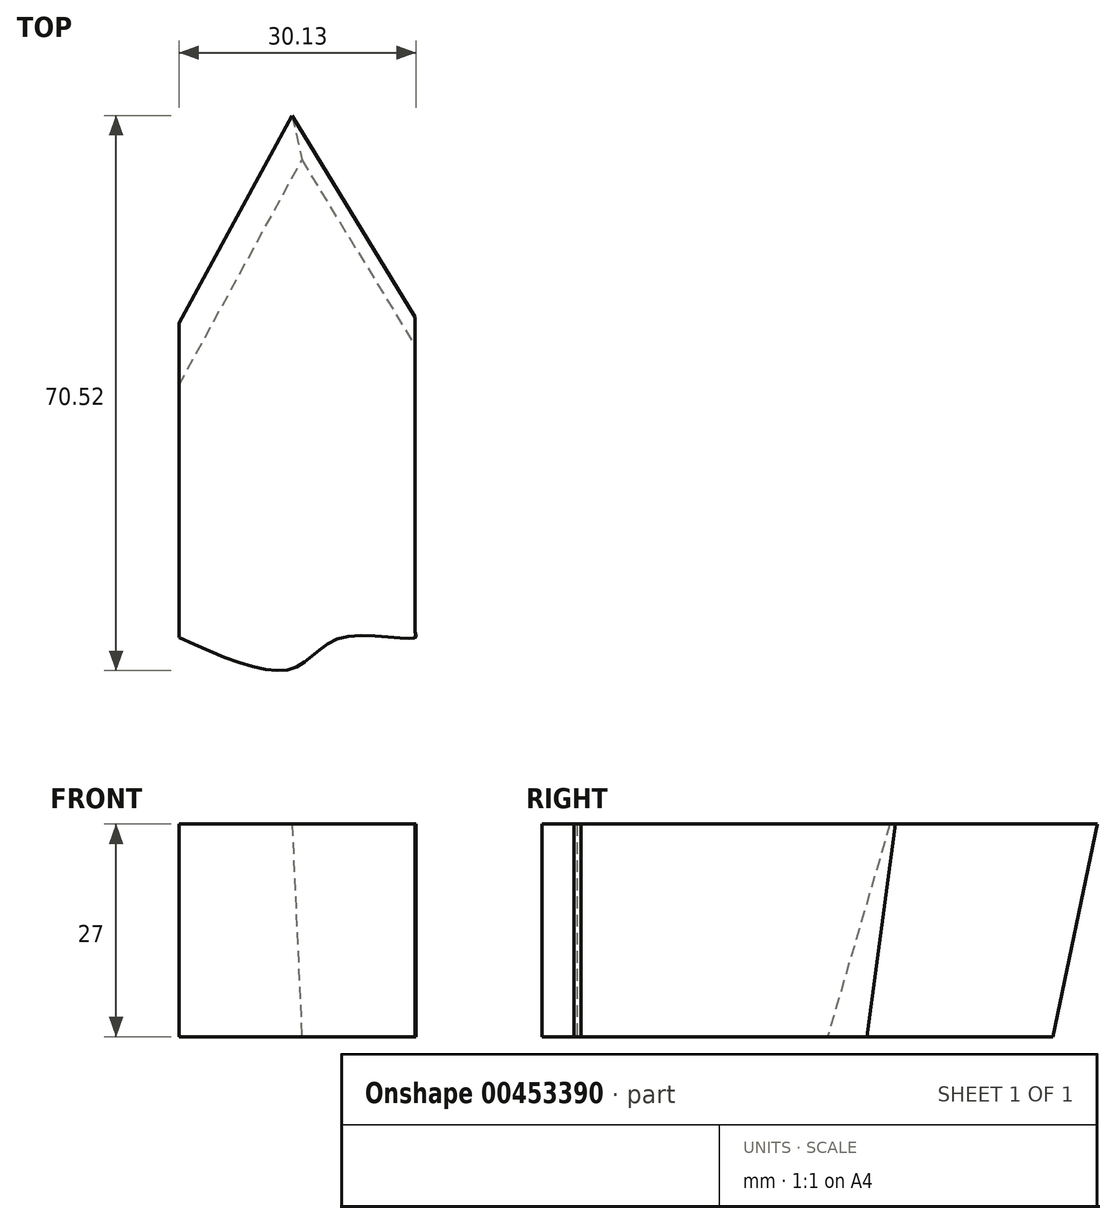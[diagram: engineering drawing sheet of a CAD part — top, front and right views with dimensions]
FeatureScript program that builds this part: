
annotation { "Feature Type Name" : "Feature", "Feature Type Description" : "" }
export const myFeature = defineFeature(function(context is Context, id is Id, definition is map)
    precondition{}
    {
        {
            var Q0;
            Q0=qCreatedBy(makeId("Top.planeOp"),FACE);
            var sketch = newSketch(context, id + "F0", { "sketchPlane" : qUnion([Q0])});
            skLineSegment(sketch, "E0", {"start": v(0, 0) * mm, "end": v(15.63, -25.6) * mm});
            skLineSegment(sketch, "E1", {"start": v(0, 0) * mm, "end": v(-14.37, -26.34) * mm});
            skLineSegment(sketch, "E2", {"start": v(-14.37, -26.34) * mm, "end": v(-14.37, -66.34) * mm});
            skLineSegment(sketch, "E3", {"start": v(15.63, -25.6) * mm, "end": v(15.63, -65.6) * mm});
            skFitSpline(sketch, "E4", {"points": [v(-14.37, -66.34) * mm, v(0, -70.28) * mm, v(6.3, -66.34) * mm, v(15.63, -66.34) * mm, v(15.63, -65.6) * mm], "startDerivative": vector(45.3, -20.27) * mm, "endDerivative": vector(-4.3, 10.74) * mm});
            skSolve(sketch);
        }
        {
            var Q0;
            Q0 = qSketchRegion(id + "F0", true);
            var Q1;
            Q1=makeQuery(id+"F0.imprint","IMPRINT",FACE,{"disambiguationData":[TD([[makeQuery(id+"F0.imprint","IMPRINT",EDGE,{"derivedFrom":sQuery(id+"F0.wireOp",EDGE,"E0")}),-1.0]])]});
            extrude(context, id + "F1", {"entities" : qUnion([Q0, Q1]), "oppositeDirection" : true, "depth" : 27 * mm});
        }
        {
            var Q0;
            Q0=makeQuery(id+"F1.opExtrude","CAP_EDGE",EDGE,{"disambiguationData":[OSD([sQuery(id+"F0.wireOp",EDGE,"E0")])],"isStart":false});
            chamfer(context, id + "F2", {"entities" : qUnion([Q0]), "chamferType" : ChamferType.OFFSET_ANGLE, "width" : 27 * mm, "oppositeDirection" : true, "angle" : 4 * degree, "tangentPropagation" : true});
        }
        {
            var Q0;
            Q0=makeQuery(id+"F1.opExtrude","CAP_EDGE",EDGE,{"disambiguationData":[OSD([sQuery(id+"F0.wireOp",EDGE,"E1")])],"isStart":false});
            chamfer(context, id + "F3", {"entities" : qUnion([Q0]), "chamferType" : ChamferType.OFFSET_ANGLE, "width" : 27 * mm, "oppositeDirection" : false, "angle" : 8 * degree, "tangentPropagation" : true});
        }
    });
